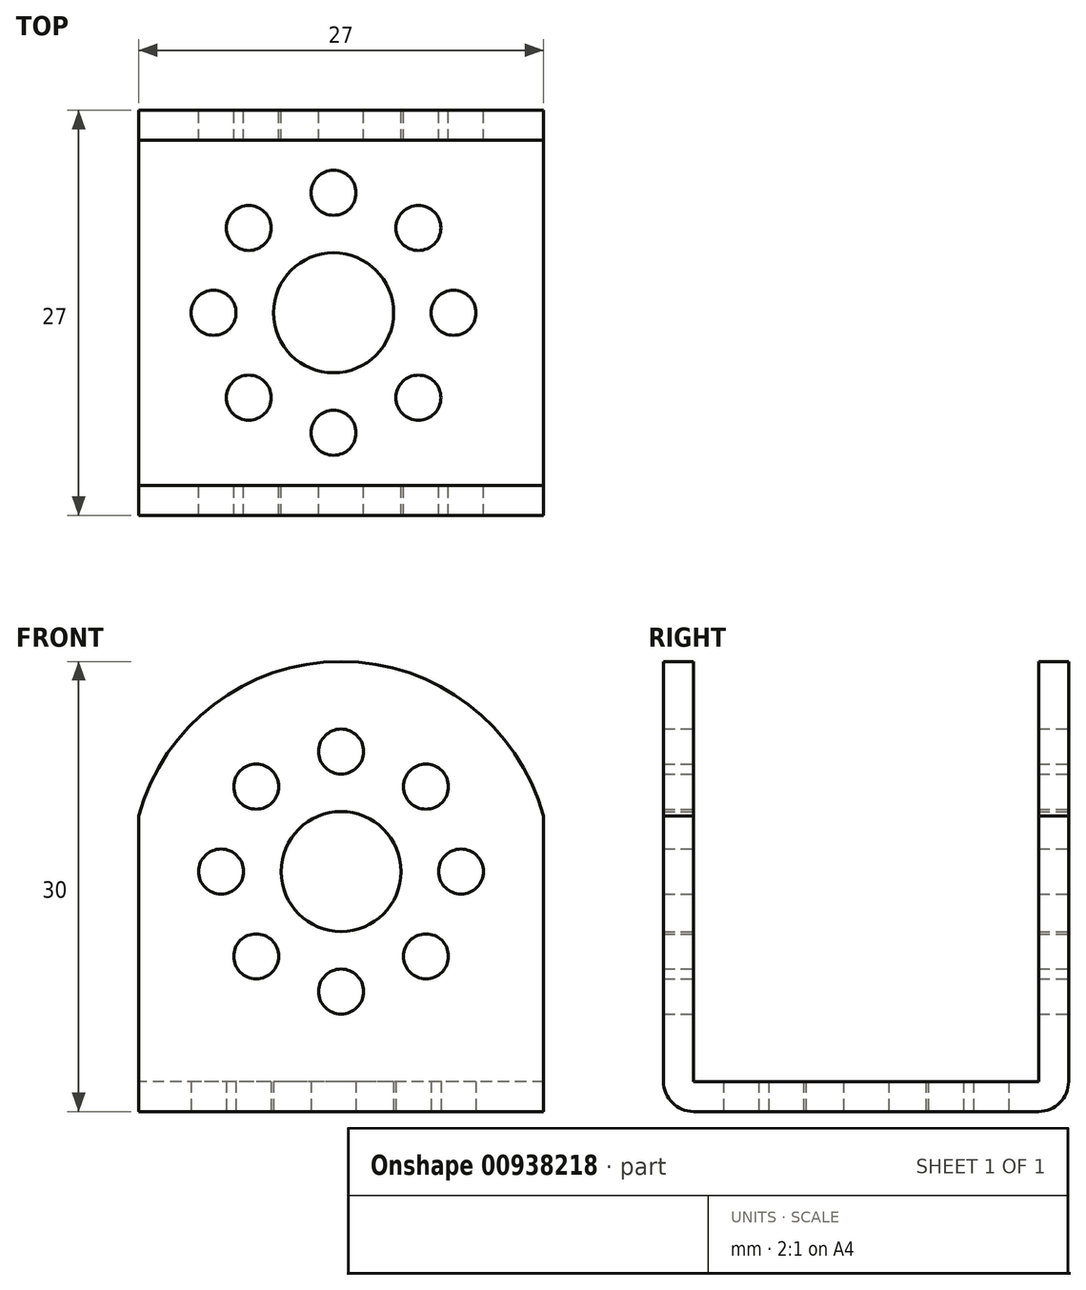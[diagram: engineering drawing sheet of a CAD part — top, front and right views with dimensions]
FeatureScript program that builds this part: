
annotation { "Feature Type Name" : "Feature", "Feature Type Description" : "" }
export const myFeature = defineFeature(function(context is Context, id is Id, definition is map)
    precondition{}
    {
        {
            var Q0;
            Q0=qCreatedBy(makeId("Right.planeOp"),FACE);
            var sketch = newSketch(context, id + "F0", { "sketchPlane" : qUnion([Q0])});
            skLineSegment(sketch, "E0.bottom", {"start": v(0, 0) * mm, "end": v(27, 0) * mm});
            skLineSegment(sketch, "E0.top", {"start": v(0, 30) * mm, "end": v(27, 30) * mm});
            skLineSegment(sketch, "E0.left", {"start": v(0, 0) * mm, "end": v(0, 30) * mm});
            skLineSegment(sketch, "E0.right", {"start": v(27, 0) * mm, "end": v(27, 30) * mm});
            skLineSegment(sketch, "E1.bottom", {"start": v(2, 30) * mm, "end": v(25, 30) * mm});
            skLineSegment(sketch, "E1.top", {"start": v(2, 2) * mm, "end": v(25, 2) * mm});
            skLineSegment(sketch, "E1.left", {"start": v(2, 30) * mm, "end": v(2, 2) * mm});
            skLineSegment(sketch, "E1.right", {"start": v(25, 30) * mm, "end": v(25, 2) * mm});
            skSolve(sketch);
        }
        {
            var Q0;
            Q0=makeQuery(id+"F0.imprint","IMPRINT",FACE,{"disambiguationData":[TD([[makeQuery(id+"F0.imprint","IMPRINT",EDGE,{"derivedFrom":sQuery(id+"F0.wireOp",EDGE,"E0.bottom")}),1.0]])]});
            extrude(context, id + "F1", {"entities" : qUnion([Q0]), "depth" : 27 * mm, "offsetDistance" : 25 * mm});
        }
        {
            var Q0;
            Q0=makeQuery(id+"F1.opExtrude","SWEPT_FACE",FACE,{"disambiguationData":[OSD([sQuery(id+"F0.wireOp",EDGE,"E0.right")])]});
            var sketch = newSketch(context, id + "F2", { "sketchPlane" : qUnion([Q0])});
            skCircle(sketch, "E2", {"center": v(-13.5, 16) * mm, "radius": 4 * mm});
            skCircle(sketch, "E3", {"center": v(-13.5, 24) * mm, "radius": 1.5 * mm});
            skCircle(sketch, "E4.1.0", {"center": v(-19.16, 21.66) * mm, "radius": 1.5 * mm});
            skCircle(sketch, "E4.2.0", {"center": v(-21.5, 16) * mm, "radius": 1.5 * mm});
            skCircle(sketch, "E4.3.0", {"center": v(-19.16, 10.34) * mm, "radius": 1.5 * mm});
            skCircle(sketch, "E4.4.0", {"center": v(-13.5, 8) * mm, "radius": 1.5 * mm});
            skCircle(sketch, "E4.5.0", {"center": v(-7.84, 10.34) * mm, "radius": 1.5 * mm});
            skCircle(sketch, "E4.6.0", {"center": v(-5.5, 16) * mm, "radius": 1.5 * mm});
            skCircle(sketch, "E4.7.0", {"center": v(-7.84, 21.66) * mm, "radius": 1.5 * mm});
            skCircle(sketch, "E5", {"center": v(-13.5, 16) * mm, "radius": 14 * mm});
            skSolve(sketch);
        }
        {
            var Q0;
            Q0=makeQuery(id+"F2.imprint","IMPRINT",FACE,{"disambiguationData":[TD([[makeQuery(id+"F2.imprint","IMPRINT",EDGE,{"derivedFrom":sQuery(id+"F2.wireOp",EDGE,"E3")}),1.0]])]});
            var Q1;
            Q1=makeQuery(id+"F2.imprint","IMPRINT",FACE,{"disambiguationData":[TD([[makeQuery(id+"F2.imprint","IMPRINT",EDGE,{"derivedFrom":sQuery(id+"F2.wireOp",EDGE,"E4.7.0")}),1.0]])]});
            var Q2;
            Q2=makeQuery(id+"F2.imprint","IMPRINT",FACE,{"disambiguationData":[TD([[makeQuery(id+"F2.imprint","IMPRINT",EDGE,{"derivedFrom":sQuery(id+"F2.wireOp",EDGE,"E4.6.0")}),1.0]])]});
            var Q3;
            Q3=makeQuery(id+"F2.imprint","IMPRINT",FACE,{"disambiguationData":[TD([[makeQuery(id+"F2.imprint","IMPRINT",EDGE,{"derivedFrom":sQuery(id+"F2.wireOp",EDGE,"E4.5.0")}),1.0]])]});
            var Q4;
            Q4=makeQuery(id+"F2.imprint","IMPRINT",FACE,{"disambiguationData":[TD([[makeQuery(id+"F2.imprint","IMPRINT",EDGE,{"derivedFrom":sQuery(id+"F2.wireOp",EDGE,"E4.4.0")}),1.0]])]});
            var Q5;
            Q5=makeQuery(id+"F2.imprint","IMPRINT",FACE,{"disambiguationData":[TD([[makeQuery(id+"F2.imprint","IMPRINT",EDGE,{"derivedFrom":sQuery(id+"F2.wireOp",EDGE,"E4.3.0")}),1.0]])]});
            var Q6;
            Q6=makeQuery(id+"F2.imprint","IMPRINT",FACE,{"disambiguationData":[TD([[makeQuery(id+"F2.imprint","IMPRINT",EDGE,{"derivedFrom":sQuery(id+"F2.wireOp",EDGE,"E4.2.0")}),1.0]])]});
            var Q7;
            Q7=makeQuery(id+"F2.imprint","IMPRINT",FACE,{"disambiguationData":[TD([[makeQuery(id+"F2.imprint","IMPRINT",EDGE,{"derivedFrom":sQuery(id+"F2.wireOp",EDGE,"E2")}),1.0]])]});
            var Q8;
            Q8=makeQuery(id+"F2.imprint","IMPRINT",FACE,{"disambiguationData":[TD([[makeQuery(id+"F2.imprint","IMPRINT",EDGE,{"derivedFrom":sQuery(id+"F2.wireOp",EDGE,"E4.1.0")}),1.0]])]});
            extrude(context, id + "F3", {"entities" : qUnion([Q0, Q1, Q2, Q3, Q4, Q5, Q6, Q7, Q8]), "operationType" : NewBodyOperationType.REMOVE, "endBound" : BoundingType.THROUGH_ALL, "oppositeDirection" : true, "depth" : 25 * mm, "offsetDistance" : 25 * mm});
        }
        {
            var Q0;
            Q0=makeQuery(id+"F1.opExtrude","SWEPT_FACE",FACE,{"disambiguationData":[OSD([sQuery(id+"F0.wireOp",EDGE,"E0.right")])]});
            var sketch = newSketch(context, id + "F4", { "sketchPlane" : qUnion([Q0])});
            skCircle(sketch, "E6", {"center": v(-13.5, 16) * mm, "radius": 14 * mm});
            skLineSegment(sketch, "E7.0", {"start": v(-27, 0) * mm, "end": v(-27, 30) * mm});
            skLineSegment(sketch, "E8.0", {"start": v(-27, 30) * mm, "end": v(0, 30) * mm});
            skLineSegment(sketch, "E9.0", {"start": v(0, 0) * mm, "end": v(0, 30) * mm});
            skSolve(sketch);
        }
        {
            var Q0;
            {var subQ0=sQuery(id+"F4.wireOp",EDGE,"E8.0");var subQ1=sQuery(id+"F4.wireOp",EDGE,"E6");var subQ2=makeQuery(id+"F4.imprint","INTERSECT",VERTEX,{"derivedFrom":[subQ1,subQ0]});Q0=makeQuery(id+"F4.imprint","IMPRINT",FACE,{"disambiguationData":[TD([[makeQuery(id+"F4.imprint","IMPRINT",EDGE,{"disambiguationData":[TD([[subQ2,-1.0]])],"derivedFrom":subQ1}),-1.0]])]});}
            var Q1;
            {var subQ0=sQuery(id+"F4.wireOp",EDGE,"E8.0");var subQ1=sQuery(id+"F4.wireOp",EDGE,"E6");var subQ2=makeQuery(id+"F4.imprint","INTERSECT",VERTEX,{"derivedFrom":[subQ1,subQ0]});Q1=makeQuery(id+"F4.imprint","IMPRINT",FACE,{"disambiguationData":[TD([[makeQuery(id+"F4.imprint","IMPRINT",EDGE,{"disambiguationData":[TD([[subQ2,1.0]])],"derivedFrom":subQ1}),-1.0]])]});}
            extrude(context, id + "F5", {"entities" : qUnion([Q0, Q1]), "operationType" : NewBodyOperationType.REMOVE, "endBound" : BoundingType.THROUGH_ALL, "oppositeDirection" : true, "depth" : 25 * mm, "offsetDistance" : 25 * mm});
        }
        {
            var Q0;
            {var subQ1=sQuery(id+"F0.wireOp",EDGE,"E0.left");var subQ2=sQuery(id+"F4.wireOp",EDGE,"E6");var subQ4=sQuery(id+"F4.wireOp",EDGE,"E7.0");Q0=makeQuery(id+"F5.boolean.opBoolean","COPY",EDGE,{"disambiguationData":[TD([makeQuery(id+"F1.opExtrude","SWEPT_FACE",FACE,{"disambiguationData":[OSD([subQ1])]})])],"derivedFrom":makeQuery(id+"F5.opExtrude","SWEPT_EDGE",EDGE,{"disambiguationData":[OSD([subQ2,subQ4])]})});}
            var Q1;
            {var subQ0=sQuery(id+"F4.wireOp",EDGE,"E6");var subQ2=sQuery(id+"F4.wireOp",EDGE,"E9.0");var subQ4=sQuery(id+"F0.wireOp",EDGE,"E0.left");Q1=makeQuery(id+"F5.boolean.opBoolean","COPY",EDGE,{"disambiguationData":[TD([makeQuery(id+"F1.opExtrude","SWEPT_FACE",FACE,{"disambiguationData":[OSD([subQ4])]})])],"derivedFrom":makeQuery(id+"F5.opExtrude","SWEPT_EDGE",EDGE,{"disambiguationData":[OSD([subQ0,subQ2])]})});}
            var Q2;
            {var subQ0=sQuery(id+"F4.wireOp",EDGE,"E6");var subQ2=sQuery(id+"F4.wireOp",EDGE,"E9.0");var subQ3=sQuery(id+"F0.wireOp",EDGE,"E0.right");Q2=makeQuery(id+"F5.boolean.opBoolean","COPY",EDGE,{"disambiguationData":[TD([makeQuery(id+"F1.opExtrude","SWEPT_FACE",FACE,{"disambiguationData":[OSD([subQ3])]})])],"derivedFrom":makeQuery(id+"F5.opExtrude","SWEPT_EDGE",EDGE,{"disambiguationData":[OSD([subQ0,subQ2])]})});}
            var Q3;
            {var subQ1=sQuery(id+"F4.wireOp",EDGE,"E6");var subQ3=sQuery(id+"F4.wireOp",EDGE,"E7.0");var subQ4=sQuery(id+"F0.wireOp",EDGE,"E0.right");Q3=makeQuery(id+"F5.boolean.opBoolean","COPY",EDGE,{"disambiguationData":[TD([makeQuery(id+"F1.opExtrude","SWEPT_FACE",FACE,{"disambiguationData":[OSD([subQ4])]})])],"derivedFrom":makeQuery(id+"F5.opExtrude","SWEPT_EDGE",EDGE,{"disambiguationData":[OSD([subQ1,subQ3])]})});}
            var Q4;
            Q4=makeQuery(id+"F1.opExtrude","SWEPT_EDGE",EDGE,{"disambiguationData":[OSD([sQuery(id+"F0.wireOp",EDGE,"E0.bottom"),sQuery(id+"F0.wireOp",EDGE,"E0.right")])]});
            var Q5;
            Q5=makeQuery(id+"F1.opExtrude","SWEPT_EDGE",EDGE,{"disambiguationData":[OSD([sQuery(id+"F0.wireOp",EDGE,"E0.bottom"),sQuery(id+"F0.wireOp",EDGE,"E0.left")])]});
            fillet(context, id + "F6", {"entities" : qUnion([Q0, Q1, Q2, Q3, Q4, Q5]), "radius" : 2 * mm, "tangentPropagation" : true, "allowEdgeOverflow" : false});
        }
        {
            var Q0;
            Q0=makeQuery(id+"F1.opExtrude","SWEPT_FACE",FACE,{"disambiguationData":[OSD([sQuery(id+"F0.wireOp",EDGE,"E0.bottom")])]});
            var sketch = newSketch(context, id + "F7", { "sketchPlane" : qUnion([Q0])});
            skCircle(sketch, "E10", {"center": v(13, -13.5) * mm, "radius": 4 * mm});
            skCircle(sketch, "E11", {"center": v(13, -5.5) * mm, "radius": 1.5 * mm});
            skCircle(sketch, "E12.1.0", {"center": v(7.34, -7.84) * mm, "radius": 1.5 * mm});
            skCircle(sketch, "E12.2.0", {"center": v(5, -13.5) * mm, "radius": 1.5 * mm});
            skCircle(sketch, "E12.3.0", {"center": v(7.34, -19.16) * mm, "radius": 1.5 * mm});
            skCircle(sketch, "E12.4.0", {"center": v(13, -21.5) * mm, "radius": 1.5 * mm});
            skCircle(sketch, "E12.5.0", {"center": v(18.66, -19.16) * mm, "radius": 1.5 * mm});
            skCircle(sketch, "E12.6.0", {"center": v(21, -13.5) * mm, "radius": 1.5 * mm});
            skCircle(sketch, "E12.7.0", {"center": v(18.66, -7.84) * mm, "radius": 1.5 * mm});
            skSolve(sketch);
        }
        {
            var Q0;
            Q0=makeQuery(id+"F7.imprint","IMPRINT",FACE,{"disambiguationData":[TD([[makeQuery(id+"F7.imprint","IMPRINT",EDGE,{"derivedFrom":sQuery(id+"F7.wireOp",EDGE,"E10")}),1.0]])]});
            var Q1;
            Q1=makeQuery(id+"F7.imprint","IMPRINT",FACE,{"disambiguationData":[TD([[makeQuery(id+"F7.imprint","IMPRINT",EDGE,{"derivedFrom":sQuery(id+"F7.wireOp",EDGE,"E12.6.0")}),1.0]])]});
            var Q2;
            Q2=makeQuery(id+"F7.imprint","IMPRINT",FACE,{"disambiguationData":[TD([[makeQuery(id+"F7.imprint","IMPRINT",EDGE,{"derivedFrom":sQuery(id+"F7.wireOp",EDGE,"E12.5.0")}),1.0]])]});
            var Q3;
            Q3=makeQuery(id+"F7.imprint","IMPRINT",FACE,{"disambiguationData":[TD([[makeQuery(id+"F7.imprint","IMPRINT",EDGE,{"derivedFrom":sQuery(id+"F7.wireOp",EDGE,"E12.4.0")}),1.0]])]});
            var Q4;
            Q4=makeQuery(id+"F7.imprint","IMPRINT",FACE,{"disambiguationData":[TD([[makeQuery(id+"F7.imprint","IMPRINT",EDGE,{"derivedFrom":sQuery(id+"F7.wireOp",EDGE,"E12.3.0")}),1.0]])]});
            var Q5;
            Q5=makeQuery(id+"F7.imprint","IMPRINT",FACE,{"disambiguationData":[TD([[makeQuery(id+"F7.imprint","IMPRINT",EDGE,{"derivedFrom":sQuery(id+"F7.wireOp",EDGE,"E12.2.0")}),1.0]])]});
            var Q6;
            Q6=makeQuery(id+"F7.imprint","IMPRINT",FACE,{"disambiguationData":[TD([[makeQuery(id+"F7.imprint","IMPRINT",EDGE,{"derivedFrom":sQuery(id+"F7.wireOp",EDGE,"E12.1.0")}),1.0]])]});
            var Q7;
            Q7=makeQuery(id+"F7.imprint","IMPRINT",FACE,{"disambiguationData":[TD([[makeQuery(id+"F7.imprint","IMPRINT",EDGE,{"derivedFrom":sQuery(id+"F7.wireOp",EDGE,"E11")}),1.0]])]});
            var Q8;
            Q8=makeQuery(id+"F7.imprint","IMPRINT",FACE,{"disambiguationData":[TD([[makeQuery(id+"F7.imprint","IMPRINT",EDGE,{"derivedFrom":sQuery(id+"F7.wireOp",EDGE,"E12.7.0")}),1.0]])]});
            extrude(context, id + "F8", {"entities" : qUnion([Q0, Q1, Q2, Q3, Q4, Q5, Q6, Q7, Q8]), "operationType" : NewBodyOperationType.REMOVE, "oppositeDirection" : true, "depth" : 25 * mm, "offsetDistance" : 25 * mm});
        }
    });
